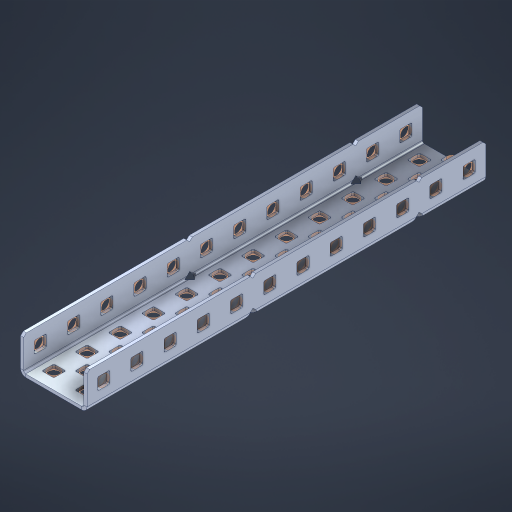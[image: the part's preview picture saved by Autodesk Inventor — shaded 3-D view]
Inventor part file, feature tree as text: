
AUTODESK INVENTOR PART (.ipt)
format: ipt  version: 2023 (Build 270158000, 158)  size: 1,030,144 bytes
history: native  units: in
note: dims shown in document units (in); Inventor stores cm internally (conversion verified against a paired STEP export)
features: other x67, extrude x58, sheet_metal_op x11, sketch x10, pattern_linear x2, mirror x1, chamfer x1
ambient origin geometry x8: Origin, YZ Plane, XZ Plane, XY Plane, X Axis, Y Axis, Z Axis, Center Point
bodies: Solid1 (feature_tree), Body (feature_tree)
feature tree (150):
  sheet_metal_op  "Flanges"
  other  "Flange Pattern Plane"
  other  "Flange Pattern Sketch"
  sheet_metal_op  "Flange Pattern"
  sheet_metal_op  "Body Pattern"
  pattern_linear  "Center Pattern"  Spacing1=0.0469in  [1 undecoded]
  other  "Arc Length"
  mirror  "Notch Mirror"
  pattern_linear  "Notch Pattern"  Spacing1=0.182in  [1 undecoded]
  chamfer  "End Chamfer"
  extrude  "Half Cut"  Depth=0.02in
  sketch  "Sketch1"  dims[d0=1.0in]
  other  "Plate1"
  sketch  "Sketch2"  dims[d1=6.0in]
  other  "Plate2"
  sheet_metal_op  "Bend1"
  sheet_metal_op  "Corner1"
  sketch  "Sketch3"  dims[d2=0.0469in]
  sketch  "Sketch7"  dims[d3=0.0469in]
  other  "Srf1"
  other  "Srf2"
  sketch  "Sketch8"  dims[d4=0.0234in]
  sketch  "Sketch9"  dims[d5=0.0938in]
  other  "Srf91"
  sheet_metal_op  "Body Pattern Sketch"
  other  "Srf92"
  sketch  "Sketch13"  dims[d6=0.0469in]
  sketch  "Sketch14"  dims[d7=0.5in d8=90.0deg d9=0.0312in]
  sketch  "Sketch15"  dims[d10=0.1875in]
  sketch  "Sketch16"  dims[d11=0.0469in d12=0.0469in d16=0.182in d17=0.02in d18=0.0469in d19=0.0in d20=0.25in d21=0.25in d38=4.7244in d40=0.5in d41=0.7874in d43=1.0in d46=0.172in d47=1.0in d48=0.0in d49=0.182in d50=0.02in d51=0.25in d52=0.25in d53=0.0469in d54=0.0in d55=0.172in d56=1.0in d57=0.0in d58=0.25in d60=4.7244in d62=0.5in d63=0.7874in d65=0.5in d85=0.1227in d86=0.1659in d88=0.04in d89=0.0469in d90=0.0in d91=0.04in d92=0.0491in d95=2.5in d96=0.04in d97=0.25in d98=45.0deg d99=0.25in d100=0.5in d101=0.0in d102=2.497in d106=0.182in d107=0.02in d108=0.5in d109=0.5in d110=0.0469in d111=0.0in d112=0.172in d113=0.5in d114=0.0in d117=0.5in d118=0.5in d119=0.5in]
  other  "Srf786"
  other  "Srf823"
  other  "Srf824"
  other  "Srf825"
  other  "Srf826"
  other  "Srf827"
  other  "Srf828"
  other  "Srf829"
  other  "Srf856"
  other  "Srf857"
  other  "Srf858"
  other  "Srf859"
  other  "Srf860"
  other  "Srf861"
  other  "Srf862"
  other  "Srf889"
  other  "Srf890"
  other  "Srf891"
  other  "Srf892"
  other  "Srf893"
  other  "Srf894"
  other  "Srf895"
  other  "Srf896"
  other  "Srf922"
  other  "Srf923"
  other  "Srf924"
  other  "Srf925"
  other  "Srf926"
  other  "Srf959"
  other  "Srf960"
  other  "Srf961"
  other  "Srf962"
  other  "Srf963"
  other  "Srf996"
  other  "Srf997"
  other  "Srf998"
  other  "Srf1143"
  other  "Srf1144"
  other  "Srf1145"
  other  "Srf1146"
  other  "Srf1147"
  other  "Srf1148"
  other  "Srf1149"
  other  "Srf1150"
  other  "Srf1151"
  other  "Srf1152"
  other  "Srf1199"
  other  "Srf1200"
  other  "Srf1201"
  other  "Srf1202"
  other  "Srf1203"
  other  "Srf1204"
  other  "Srf1205"
  other  "Srf1206"
  other  "Srf1207"
  other  "Srf1208"
  sheet_metal_op  "Flange Stamp"
  sheet_metal_op  "Flange Circle"
  sheet_metal_op  "Body Stamp"
  sheet_metal_op  "Body Circle"
  other  "Center Stamp"
  other  "Center Circle"
  sheet_metal_op  "Notch"
  extrude  "ExtrusionSrf2"  Depth=0.0469in
  extrude  "ExtrusionSrf92"  TaperAngle=0.0deg  [1 undecoded]
  extrude  "ExtrusionSrf823"  Depth=0.5in
  extrude  "ExtrusionSrf824"  Depth=0.5in
  extrude  "ExtrusionSrf825"  Depth=0.5in
  extrude  "ExtrusionSrf826"  Depth=0.5in
  extrude  "ExtrusionSrf827"  Depth=1.0in TaperAngle=0.0deg
  extrude  "ExtrusionSrf828"  Depth=0.5in
  extrude  "ExtrusionSrf829"  Depth=0.02in
  extrude  "ExtrusionSrf856"  Depth=0.5in
  extrude  "ExtrusionSrf857"  Depth=0.5in
  extrude  "ExtrusionSrf858"  Depth=0.0469in
  extrude  "ExtrusionSrf859"  TaperAngle=0.0deg  [1 undecoded]
  extrude  "ExtrusionSrf860"  Depth=0.5in
  extrude  "ExtrusionSrf861"  Depth=1.0in TaperAngle=0.0deg
  extrude  "ExtrusionSrf862"  Depth=0.5in
  extrude  "ExtrusionSrf889"  Depth=0.5in
  extrude  "ExtrusionSrf890"  Depth=0.5in
  extrude  "ExtrusionSrf891"  Depth=0.5in
  extrude  "ExtrusionSrf892"  Depth=0.5in
  extrude  "ExtrusionSrf893"  Depth=0.5in
  extrude  "ExtrusionSrf894"  Depth=0.0469in
  extrude  "ExtrusionSrf895"  TaperAngle=0.0deg  [1 undecoded]
  extrude  "ExtrusionSrf896"  Depth=0.5in
  extrude  "ExtrusionSrf922"  Depth=0.5in
  extrude  "ExtrusionSrf923"  Depth=2.5in
  extrude  "ExtrusionSrf924"  Depth=0.5in TaperAngle=45.0deg
  extrude  "ExtrusionSrf925"  Depth=0.5in
  extrude  "ExtrusionSrf926"  Depth=0.5in TaperAngle=0.0deg
  extrude  "ExtrusionSrf959"  Depth=0.5in
  extrude  "ExtrusionSrf960"  Depth=0.5in
  extrude  "ExtrusionSrf961"  Depth=0.02in
  extrude  "ExtrusionSrf962"  Depth=0.5in
  extrude  "ExtrusionSrf963"  Depth=0.5in
  extrude  "ExtrusionSrf996"  Depth=0.0469in
  extrude  "ExtrusionSrf997"  TaperAngle=0.0deg  [1 undecoded]
  extrude  "ExtrusionSrf998"  Depth=0.5in
  extrude  "ExtrusionSrf1143"  Depth=0.5in TaperAngle=0.0deg
  extrude  "ExtrusionSrf1144"  Depth=0.5in
  extrude  "ExtrusionSrf1145"  Depth=0.5in
  extrude  "ExtrusionSrf1146"  Depth=0.5in
  extrude  "ExtrusionSrf1147"  [1 undecoded]
  extrude  "ExtrusionSrf1148"  [1 undecoded]
  extrude  "ExtrusionSrf1149"  [1 undecoded]
  extrude  "ExtrusionSrf1150"  [1 undecoded]
  extrude  "ExtrusionSrf1151"  [1 undecoded]
  extrude  "ExtrusionSrf1152"  [1 undecoded]
  extrude  "ExtrusionSrf1199"  [1 undecoded]
  extrude  "ExtrusionSrf1200"  [1 undecoded]
  extrude  "ExtrusionSrf1201"  [1 undecoded]
  extrude  "ExtrusionSrf1202"  [1 undecoded]
  extrude  "ExtrusionSrf1203"  [1 undecoded]
  extrude  "ExtrusionSrf1204"  [1 undecoded]
  extrude  "ExtrusionSrf1205"  [1 undecoded]
  extrude  "ExtrusionSrf1206"  [1 undecoded]
  extrude  "ExtrusionSrf1207"  [1 undecoded]
  extrude  "ExtrusionSrf1208"  [1 undecoded]
note: 22 required parameter values undecoded (feature->parameter linkage not recoverable at this tier; creation-order binding heuristic only, values carry confidence <= 0.55)
